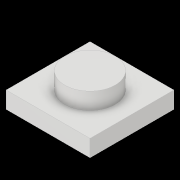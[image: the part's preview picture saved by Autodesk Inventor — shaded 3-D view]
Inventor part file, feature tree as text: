
AUTODESK INVENTOR PART (.ipt)
format: ipt  version: 2019 (Build 230136000, 136)  size: 107,520 bytes
history: native  units: mm
features: extrude x2, sketch x2, other x1
ambient origin geometry x8: Origin, YZ Plane, XZ Plane, XY Plane, X Axis, Y Axis, Z Axis, Center Point
bodies: Body1 (feature_tree)
feature tree (5):
  other  "솔리드1"
  extrude  "돌출1"  Depth=50.0mm
  extrude  "돌출2"  Depth=50.0mm
  sketch  "스케치1"
  sketch  "스케치2"
